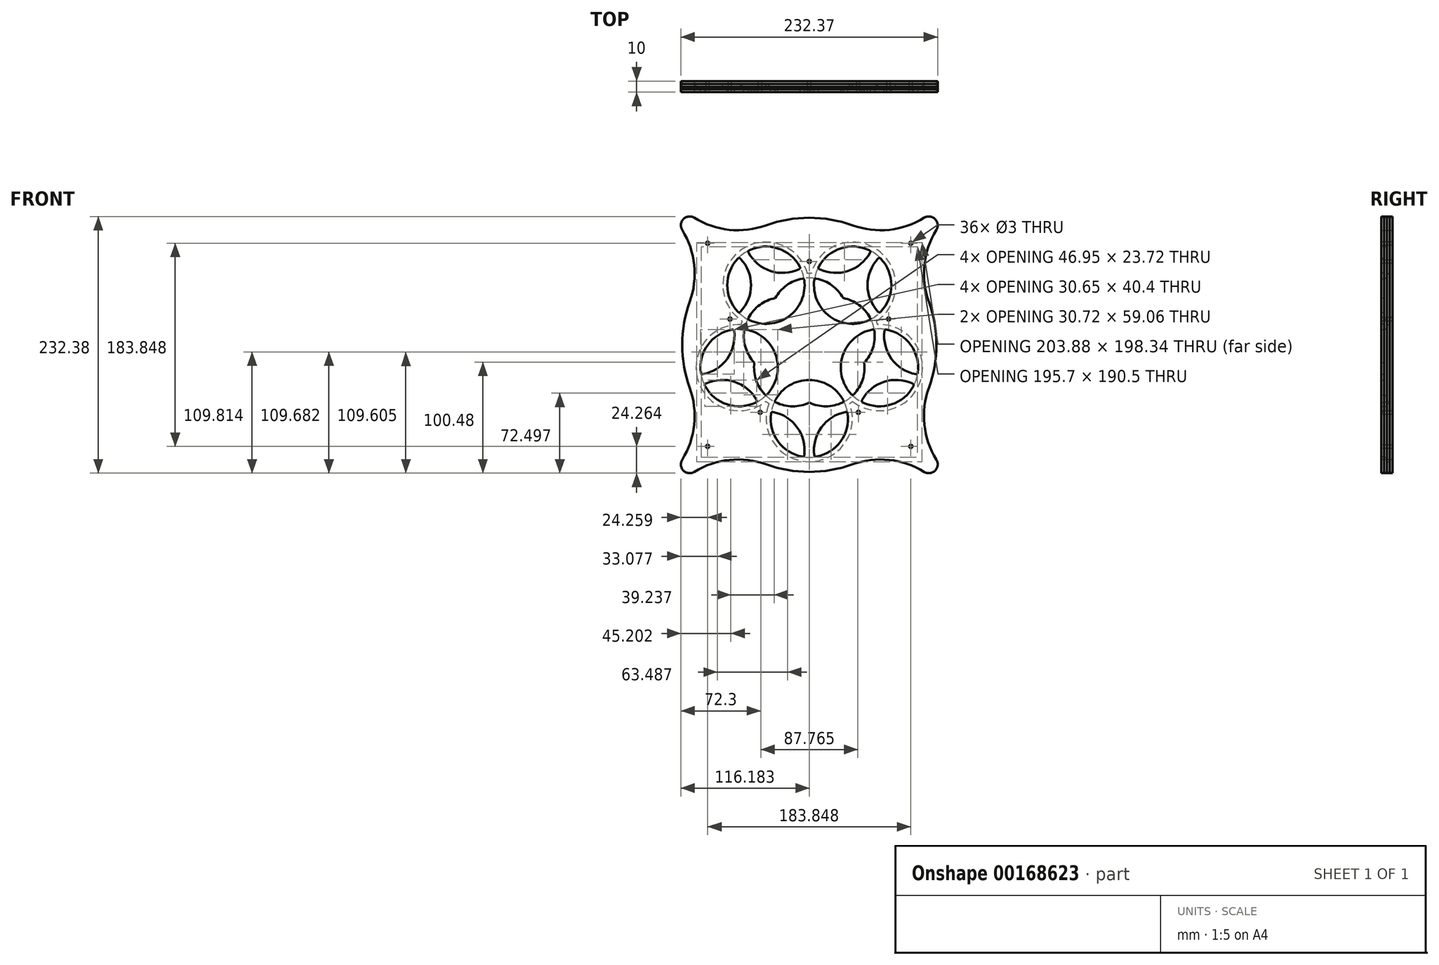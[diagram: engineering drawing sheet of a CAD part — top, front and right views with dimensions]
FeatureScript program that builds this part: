
annotation { "Feature Type Name" : "Feature", "Feature Type Description" : "" }
export const myFeature = defineFeature(function(context is Context, id is Id, definition is map)
    precondition{}
    {
        {
            var Q0;
            Q0=qCreatedBy(makeId("Front.planeOp"),FACE);
            var sketch = newSketch(context, id + "F0", { "sketchPlane" : qUnion([Q0])});
            skCircle(sketch, "E0", {"center": v(0, 0) * mm, "radius": 35 * mm});
            skLineSegment(sketch, "E1", {"start": v(0, 0) * mm, "end": v(48.5, 0) * mm});
            skCircle(sketch, "E2", {"center": v(48.5, 0) * mm, "radius": 35 * mm});
            skCircle(sketch, "E3.3.0", {"center": v(-14.99, 46.13) * mm, "radius": 35 * mm});
            skCircle(sketch, "E3.4.0", {"center": v(-39.24, 28.5) * mm, "radius": 35 * mm});
            skCircle(sketch, "E3.7.0", {"center": v(-14.99, -46.13) * mm, "radius": 35 * mm});
            skLineSegment(sketch, "E4", {"start": v(-34.45, -6.16) * mm, "end": v(-4.78, 34.67) * mm, "construction": true});
            skCircle(sketch, "E5.MirrorC", {"center": v(9.26, 28.5) * mm, "radius": 35 * mm});
            skLineSegment(sketch, "E6", {"start": v(0, 0) * mm, "end": v(9.26, 28.5) * mm});
            skLineSegment(sketch, "E7", {"start": v(0, 0) * mm, "end": v(-19.62, 14.25) * mm, "construction": true});
            skLineSegment(sketch, "E8", {"start": v(0, 0) * mm, "end": v(-29.97, 0) * mm, "construction": true});
            skCircle(sketch, "E9", {"center": v(-29.97, 0) * mm, "radius": 35 * mm});
            skLineSegment(sketch, "E10", {"start": v(24.25, 25.24) * mm, "end": v(24.25, -25.24) * mm, "construction": true});
            skCircle(sketch, "E11.MirrorC", {"center": v(63.49, -46.13) * mm, "radius": 35 * mm});
            skCircle(sketch, "E12.MirrorC", {"center": v(87.74, 28.5) * mm, "radius": 35 * mm});
            skLineSegment(sketch, "E13", {"start": v(-14.99, 31.63) * mm, "end": v(-14.99, -31.63) * mm, "construction": true});
            skCircle(sketch, "E14.MirrorC", {"center": v(-78.47, 0) * mm, "radius": 35 * mm});
            skSolve(sketch);
        }
        {
            var Q0;
            Q0=qCreatedBy(makeId("Front.planeOp"),FACE);
            var sketch = newSketch(context, id + "F1", { "sketchPlane" : qUnion([Q0])});
            skArc(sketch, "E15.0", {"start": v(-10.2, 80.8) * mm, "mid": v(-14.99, 81.13) * mm, "end": v(-19.77, 80.8) * mm});
            skArc(sketch, "E15.1", {"start": v(40.76, 43.77) * mm, "mid": v(42.55, 39.32) * mm, "end": v(43.72, 34.67) * mm});
            skArc(sketch, "E15.2", {"start": v(-70.73, 43.77) * mm, "mid": v(-72.52, 39.32) * mm, "end": v(-73.7, 34.67) * mm});
            skArc(sketch, "E15.3", {"start": v(-54.22, -25.24) * mm, "mid": v(-50.55, -28.32) * mm, "end": v(-46.48, -30.86) * mm});
            skArc(sketch, "E15.4", {"start": v(16.5, -30.86) * mm, "mid": v(20.57, -28.32) * mm, "end": v(24.25, -25.24) * mm});
            skArc(sketch, "E15.5", {"start": v(-46.48, -30.86) * mm, "mid": v(-14.99, -81.13) * mm, "end": v(16.5, -30.86) * mm});
            skLineSegment(sketch, "E16", {"start": v(-64.69, 4.48) * mm, "end": v(42.55, 39.32) * mm, "construction": true});
            skLineSegment(sketch, "E17", {"start": v(34.71, 4.48) * mm, "end": v(-72.52, 39.32) * mm, "construction": true});
            skPoint(sketch, "E18", {"position": v(-14.99, 20.63) * mm});
            skArc(sketch, "E19.1.0", {"start": v(24.25, -25.24) * mm, "mid": v(81.79, -10.82) * mm, "end": v(43.72, 34.67) * mm});
            skArc(sketch, "E19.2.0", {"start": v(40.76, 43.77) * mm, "mid": v(44.82, 102.95) * mm, "end": v(-10.2, 80.8) * mm});
            skArc(sketch, "E19.3.0", {"start": v(-19.77, 80.8) * mm, "mid": v(-74.8, 102.95) * mm, "end": v(-70.73, 43.77) * mm});
            skArc(sketch, "E19.4.0", {"start": v(-73.7, 34.67) * mm, "mid": v(-111.76, -10.82) * mm, "end": v(-54.22, -25.24) * mm});
            skLineSegment(sketch, "E20", {"start": v(-14.99, 20.63) * mm, "end": v(-14.99, -81.13) * mm, "construction": true});
            skLineSegment(sketch, "E21", {"start": v(-14.99, 20.63) * mm, "end": v(93.2, -87.56) * mm, "construction": true});
            skArc(sketch, "E22", {"start": v(88.99, -94.36) * mm, "mid": v(98.86, -93.22) * mm, "end": v(100, -83.34) * mm});
            skArc(sketch, "E23", {"start": v(93.2, -18.38) * mm, "mid": v(100.01, 20.63) * mm, "end": v(93.2, 59.64) * mm});
            skArc(sketch, "E24", {"start": v(93.2, -18.38) * mm, "mid": v(89.15, -51.64) * mm, "end": v(100, -83.34) * mm});
            skArc(sketch, "E25.MirrorCS", {"start": v(24.03, -87.55) * mm, "mid": v(57.29, -83.51) * mm, "end": v(88.99, -94.36) * mm});
            skArc(sketch, "E26.1.0", {"start": v(93.2, 59.64) * mm, "mid": v(89.15, 92.9) * mm, "end": v(100, 124.6) * mm});
            skArc(sketch, "E26.1.1", {"start": v(100, 124.6) * mm, "mid": v(98.86, 134.47) * mm, "end": v(88.99, 135.62) * mm});
            skArc(sketch, "E26.1.2", {"start": v(24.03, 128.8) * mm, "mid": v(57.29, 124.77) * mm, "end": v(88.99, 135.62) * mm});
            skArc(sketch, "E26.2.0", {"start": v(-54, 128.8) * mm, "mid": v(-87.26, 124.77) * mm, "end": v(-118.96, 135.62) * mm});
            skArc(sketch, "E26.2.1", {"start": v(-118.96, 135.62) * mm, "mid": v(-128.83, 134.47) * mm, "end": v(-129.97, 124.6) * mm});
            skArc(sketch, "E26.2.2", {"start": v(-123.17, 59.64) * mm, "mid": v(-119.13, 92.9) * mm, "end": v(-129.97, 124.6) * mm});
            skArc(sketch, "E26.3.0", {"start": v(-123.17, -18.38) * mm, "mid": v(-119.13, -51.64) * mm, "end": v(-129.97, -83.34) * mm});
            skArc(sketch, "E26.3.1", {"start": v(-129.97, -83.34) * mm, "mid": v(-128.83, -93.22) * mm, "end": v(-118.96, -94.36) * mm});
            skArc(sketch, "E26.3.2", {"start": v(-54, -87.55) * mm, "mid": v(-87.26, -83.51) * mm, "end": v(-118.96, -94.36) * mm});
            skArc(sketch, "E27.trimOffspring", {"start": v(-54, -87.55) * mm, "mid": v(-14.99, -94.37) * mm, "end": v(24.03, -87.55) * mm});
            skArc(sketch, "E28.trimOffspring", {"start": v(-123.17, 59.64) * mm, "mid": v(-129.99, 20.63) * mm, "end": v(-123.17, -18.38) * mm});
            skArc(sketch, "E29.trimOffspring", {"start": v(24.03, 128.8) * mm, "mid": v(-14.99, 135.63) * mm, "end": v(-54, 128.8) * mm});
            skSolve(sketch);
        }
        {
            var Q0;
            Q0=makeQuery(id+"F1.imprint","IMPRINT",FACE,{"disambiguationData":[TD([[makeQuery(id+"F1.imprint","IMPRINT",EDGE,{"derivedFrom":sQuery(id+"F1.wireOp",EDGE,"E15.0")}),-1.0]])]});
            var Q1;
            Q1=makeQuery(id+"F1.imprint","IMPRINT",FACE,{"disambiguationData":[TD([[makeQuery(id+"F1.imprint","IMPRINT",EDGE,{"derivedFrom":sQuery(id+"F1.wireOp",EDGE,"E15.0")}),1.0]])]});
            extrude(context, id + "F2", {"entities" : qUnion([Q0, Q1]), "depth" : 2.5 * mm});
        }
        {
            var Q0;
            Q0=makeQuery(id+"F2.opExtrude","CAP_FACE",FACE,{"disambiguationData":[OSD([sQuery(id+"F1.wireOp",EDGE,"E22"),sQuery(id+"F1.wireOp",EDGE,"E23"),sQuery(id+"F1.wireOp",EDGE,"E24"),sQuery(id+"F1.wireOp",EDGE,"E25.MirrorCS"),sQuery(id+"F1.wireOp",EDGE,"E26.1.0"),sQuery(id+"F1.wireOp",EDGE,"E26.1.1"),sQuery(id+"F1.wireOp",EDGE,"E26.1.2"),sQuery(id+"F1.wireOp",EDGE,"E26.2.0"),sQuery(id+"F1.wireOp",EDGE,"E26.2.1"),sQuery(id+"F1.wireOp",EDGE,"E26.2.2"),sQuery(id+"F1.wireOp",EDGE,"E26.3.0"),sQuery(id+"F1.wireOp",EDGE,"E26.3.1"),sQuery(id+"F1.wireOp",EDGE,"E26.3.2"),sQuery(id+"F1.wireOp",EDGE,"E27.trimOffspring"),sQuery(id+"F1.wireOp",EDGE,"E28.trimOffspring"),sQuery(id+"F1.wireOp",EDGE,"E29.trimOffspring")])],"isStart":false});
            var sketch = newSketch(context, id + "F3", { "sketchPlane" : qUnion([Q0])});
            skArc(sketch, "E30.0", {"start": v(-46.48, -30.86) * mm, "mid": v(-14.99, -81.13) * mm, "end": v(16.5, -30.86) * mm, "construction": true});
            skArc(sketch, "E31.0", {"start": v(24.25, -25.24) * mm, "mid": v(81.79, -10.82) * mm, "end": v(43.72, 34.67) * mm, "construction": true});
            skArc(sketch, "E32.0", {"start": v(40.76, 43.77) * mm, "mid": v(44.82, 102.95) * mm, "end": v(-10.2, 80.8) * mm, "construction": true});
            skArc(sketch, "E33.0", {"start": v(-19.77, 80.8) * mm, "mid": v(-74.8, 102.95) * mm, "end": v(-70.73, 43.77) * mm, "construction": true});
            skArc(sketch, "E34.0", {"start": v(-73.7, 34.67) * mm, "mid": v(-111.76, -10.82) * mm, "end": v(-54.22, -25.24) * mm, "construction": true});
            skArc(sketch, "E35.0", {"start": v(-70.73, 43.77) * mm, "mid": v(-72.52, 39.32) * mm, "end": v(-73.7, 34.67) * mm, "construction": true});
            skArc(sketch, "E36.0", {"start": v(-10.2, 80.8) * mm, "mid": v(-14.99, 81.13) * mm, "end": v(-19.77, 80.8) * mm, "construction": true});
            skArc(sketch, "E37.0", {"start": v(40.76, 43.77) * mm, "mid": v(42.55, 39.32) * mm, "end": v(43.72, 34.67) * mm, "construction": true});
            skArc(sketch, "E38.0", {"start": v(16.5, -30.86) * mm, "mid": v(20.57, -28.32) * mm, "end": v(24.25, -25.24) * mm, "construction": true});
            skArc(sketch, "E39.0", {"start": v(-54.22, -25.24) * mm, "mid": v(-50.55, -28.32) * mm, "end": v(-46.48, -30.86) * mm, "construction": true});
            skArc(sketch, "E40.0", {"start": v(-54.22, -30.54) * mm, "mid": v(-52.9, -31.55) * mm, "end": v(-51.53, -32.5) * mm});
            skArc(sketch, "E40.1", {"start": v(-76.8, 38.96) * mm, "mid": v(-115.57, -12.05) * mm, "end": v(-54.22, -30.54) * mm});
            skArc(sketch, "E40.2", {"start": v(-51.53, -32.5) * mm, "mid": v(-14.99, -85.13) * mm, "end": v(21.56, -32.5) * mm});
            skArc(sketch, "E40.3", {"start": v(-75.78, 42.13) * mm, "mid": v(-76.33, 40.56) * mm, "end": v(-76.8, 38.96) * mm});
            skArc(sketch, "E40.4", {"start": v(-16.65, 85.1) * mm, "mid": v(-77.15, 106.19) * mm, "end": v(-75.78, 42.13) * mm});
            skArc(sketch, "E40.5", {"start": v(-13.32, 85.1) * mm, "mid": v(-14.99, 85.13) * mm, "end": v(-16.65, 85.1) * mm});
            skArc(sketch, "E40.6", {"start": v(21.56, -32.5) * mm, "mid": v(22.92, -31.55) * mm, "end": v(24.25, -30.54) * mm});
            skArc(sketch, "E40.7", {"start": v(24.25, -30.54) * mm, "mid": v(85.6, -12.05) * mm, "end": v(46.83, 38.96) * mm});
            skArc(sketch, "E40.8", {"start": v(45.8, 42.13) * mm, "mid": v(46.35, 40.56) * mm, "end": v(46.83, 38.96) * mm});
            skArc(sketch, "E40.9", {"start": v(45.8, 42.13) * mm, "mid": v(47.17, 106.19) * mm, "end": v(-13.32, 85.1) * mm});
            skSolve(sketch);
        }
        {
            var Q0;
            Q0=makeQuery(id+"F3.imprint","IMPRINT",FACE,{"disambiguationData":[TD([[makeQuery(id+"F3.imprint","IMPRINT",EDGE,{"derivedFrom":sQuery(id+"F3.wireOp",EDGE,"E40.0")}),-1.0]])]});
            extrude(context, id + "F4", {"entities" : qUnion([Q0]), "depth" : 2.5 * mm});
        }
        {
            var Q0;
            Q0=makeQuery(id+"F4.opExtrude","CAP_FACE",FACE,{"disambiguationData":[OSD([sQuery(id+"F1.wireOp",EDGE,"E22"),sQuery(id+"F1.wireOp",EDGE,"E23"),sQuery(id+"F1.wireOp",EDGE,"E24"),sQuery(id+"F1.wireOp",EDGE,"E25.MirrorCS"),sQuery(id+"F1.wireOp",EDGE,"E26.1.0"),sQuery(id+"F1.wireOp",EDGE,"E26.1.1"),sQuery(id+"F1.wireOp",EDGE,"E26.1.2"),sQuery(id+"F1.wireOp",EDGE,"E26.2.0"),sQuery(id+"F1.wireOp",EDGE,"E26.2.1"),sQuery(id+"F1.wireOp",EDGE,"E26.2.2"),sQuery(id+"F1.wireOp",EDGE,"E26.3.0"),sQuery(id+"F1.wireOp",EDGE,"E26.3.1"),sQuery(id+"F1.wireOp",EDGE,"E26.3.2"),sQuery(id+"F1.wireOp",EDGE,"E27.trimOffspring"),sQuery(id+"F1.wireOp",EDGE,"E28.trimOffspring"),sQuery(id+"F1.wireOp",EDGE,"E29.trimOffspring"),sQuery(id+"F3.wireOp",EDGE,"E40.0"),sQuery(id+"F3.wireOp",EDGE,"E40.1"),sQuery(id+"F3.wireOp",EDGE,"E40.2"),sQuery(id+"F3.wireOp",EDGE,"E40.3"),sQuery(id+"F3.wireOp",EDGE,"E40.4"),sQuery(id+"F3.wireOp",EDGE,"E40.5"),sQuery(id+"F3.wireOp",EDGE,"E40.6"),sQuery(id+"F3.wireOp",EDGE,"E40.7"),sQuery(id+"F3.wireOp",EDGE,"E40.8"),sQuery(id+"F3.wireOp",EDGE,"E40.9")])],"isStart":false});
            var sketch = newSketch(context, id + "F5", { "sketchPlane" : qUnion([Q0])});
            skArc(sketch, "E41.0", {"start": v(-123.17, 59.64) * mm, "mid": v(-129.99, 20.63) * mm, "end": v(-123.17, -18.38) * mm});
            skArc(sketch, "E41.1", {"start": v(-123.17, 59.64) * mm, "mid": v(-119.13, 92.9) * mm, "end": v(-129.97, 124.6) * mm});
            skArc(sketch, "E41.2", {"start": v(-118.96, 135.62) * mm, "mid": v(-128.83, 134.47) * mm, "end": v(-129.97, 124.6) * mm});
            skArc(sketch, "E41.3", {"start": v(-54, 128.8) * mm, "mid": v(-87.26, 124.77) * mm, "end": v(-118.96, 135.62) * mm});
            skArc(sketch, "E41.4", {"start": v(24.03, 128.8) * mm, "mid": v(-14.99, 135.63) * mm, "end": v(-54, 128.8) * mm});
            skArc(sketch, "E41.5", {"start": v(24.03, 128.8) * mm, "mid": v(57.29, 124.77) * mm, "end": v(88.99, 135.62) * mm});
            skArc(sketch, "E41.6", {"start": v(100, 124.6) * mm, "mid": v(98.86, 134.47) * mm, "end": v(88.99, 135.62) * mm});
            skArc(sketch, "E41.7", {"start": v(93.2, 59.64) * mm, "mid": v(89.15, 92.9) * mm, "end": v(100, 124.6) * mm});
            skArc(sketch, "E41.8", {"start": v(93.2, -18.38) * mm, "mid": v(100.01, 20.63) * mm, "end": v(93.2, 59.64) * mm});
            skArc(sketch, "E41.9", {"start": v(93.2, -18.38) * mm, "mid": v(89.15, -51.64) * mm, "end": v(100, -83.34) * mm});
            skArc(sketch, "E41.10", {"start": v(88.99, -94.36) * mm, "mid": v(98.86, -93.22) * mm, "end": v(100, -83.34) * mm});
            skArc(sketch, "E41.11", {"start": v(24.03, -87.55) * mm, "mid": v(57.29, -83.51) * mm, "end": v(88.99, -94.36) * mm});
            skArc(sketch, "E41.12", {"start": v(-54, -87.55) * mm, "mid": v(-14.99, -94.37) * mm, "end": v(24.03, -87.55) * mm});
            skArc(sketch, "E41.13", {"start": v(-54, -87.55) * mm, "mid": v(-87.26, -83.51) * mm, "end": v(-118.96, -94.36) * mm});
            skArc(sketch, "E41.14", {"start": v(-129.97, -83.34) * mm, "mid": v(-128.83, -93.22) * mm, "end": v(-118.96, -94.36) * mm});
            skArc(sketch, "E41.15", {"start": v(-123.17, -18.38) * mm, "mid": v(-119.13, -51.64) * mm, "end": v(-129.97, -83.34) * mm});
            skArc(sketch, "E42.0", {"start": v(-70.73, 43.77) * mm, "mid": v(-72.52, 39.32) * mm, "end": v(-73.7, 34.67) * mm});
            skArc(sketch, "E42.1", {"start": v(-19.77, 80.8) * mm, "mid": v(-74.8, 102.95) * mm, "end": v(-70.73, 43.77) * mm});
            skArc(sketch, "E42.2", {"start": v(-10.2, 80.8) * mm, "mid": v(-14.99, 81.13) * mm, "end": v(-19.77, 80.8) * mm});
            skArc(sketch, "E42.3", {"start": v(40.76, 43.77) * mm, "mid": v(44.82, 102.95) * mm, "end": v(-10.2, 80.8) * mm});
            skArc(sketch, "E42.4", {"start": v(40.76, 43.77) * mm, "mid": v(42.55, 39.32) * mm, "end": v(43.72, 34.67) * mm});
            skArc(sketch, "E42.5", {"start": v(24.25, -25.24) * mm, "mid": v(81.79, -10.82) * mm, "end": v(43.72, 34.67) * mm});
            skArc(sketch, "E42.6", {"start": v(16.5, -30.86) * mm, "mid": v(20.57, -28.32) * mm, "end": v(24.25, -25.24) * mm});
            skArc(sketch, "E42.7", {"start": v(-46.48, -30.86) * mm, "mid": v(-14.99, -81.13) * mm, "end": v(16.5, -30.86) * mm});
            skArc(sketch, "E42.8", {"start": v(-54.22, -25.24) * mm, "mid": v(-50.55, -28.32) * mm, "end": v(-46.48, -30.86) * mm});
            skArc(sketch, "E42.9", {"start": v(-73.7, 34.67) * mm, "mid": v(-111.76, -10.82) * mm, "end": v(-54.22, -25.24) * mm});
            skSolve(sketch);
        }
        {
            var Q0;
            Q0 = qSketchRegion(id + "F5", true);
            extrude(context, id + "F6", {"entities" : qUnion([Q0]), "depth" : 2.5 * mm});
        }
        {
            var Q0;
            Q0=makeQuery(id+"F6.opExtrude","CAP_FACE",FACE,{"disambiguationData":[OSD([sQuery(id+"F5.wireOp",EDGE,"E41.0"),sQuery(id+"F5.wireOp",EDGE,"E41.1"),sQuery(id+"F5.wireOp",EDGE,"E41.2"),sQuery(id+"F5.wireOp",EDGE,"E41.3"),sQuery(id+"F5.wireOp",EDGE,"E41.4"),sQuery(id+"F5.wireOp",EDGE,"E41.5"),sQuery(id+"F5.wireOp",EDGE,"E41.6"),sQuery(id+"F5.wireOp",EDGE,"E41.7"),sQuery(id+"F5.wireOp",EDGE,"E41.8"),sQuery(id+"F5.wireOp",EDGE,"E41.9"),sQuery(id+"F5.wireOp",EDGE,"E41.10"),sQuery(id+"F5.wireOp",EDGE,"E41.11"),sQuery(id+"F5.wireOp",EDGE,"E41.12"),sQuery(id+"F5.wireOp",EDGE,"E41.13"),sQuery(id+"F5.wireOp",EDGE,"E41.14"),sQuery(id+"F5.wireOp",EDGE,"E41.15"),sQuery(id+"F5.wireOp",EDGE,"E42.0"),sQuery(id+"F5.wireOp",EDGE,"E42.1"),sQuery(id+"F5.wireOp",EDGE,"E42.2"),sQuery(id+"F5.wireOp",EDGE,"E42.3"),sQuery(id+"F5.wireOp",EDGE,"E42.4"),sQuery(id+"F5.wireOp",EDGE,"E42.5"),sQuery(id+"F5.wireOp",EDGE,"E42.6"),sQuery(id+"F5.wireOp",EDGE,"E42.7"),sQuery(id+"F5.wireOp",EDGE,"E42.8"),sQuery(id+"F5.wireOp",EDGE,"E42.9")])],"isStart":false});
            var sketch = newSketch(context, id + "F7", { "sketchPlane" : qUnion([Q0])});
            skArc(sketch, "E43.0", {"start": v(-123.17, 59.64) * mm, "mid": v(-129.99, 20.63) * mm, "end": v(-123.17, -18.38) * mm});
            skArc(sketch, "E43.1", {"start": v(-123.17, 59.64) * mm, "mid": v(-119.13, 92.9) * mm, "end": v(-129.97, 124.6) * mm});
            skArc(sketch, "E43.2", {"start": v(-118.96, 135.62) * mm, "mid": v(-128.83, 134.47) * mm, "end": v(-129.97, 124.6) * mm});
            skArc(sketch, "E43.3", {"start": v(-54, 128.8) * mm, "mid": v(-87.26, 124.77) * mm, "end": v(-118.96, 135.62) * mm});
            skArc(sketch, "E43.4", {"start": v(24.03, 128.8) * mm, "mid": v(-14.99, 135.63) * mm, "end": v(-54, 128.8) * mm});
            skArc(sketch, "E43.5", {"start": v(24.03, 128.8) * mm, "mid": v(57.29, 124.77) * mm, "end": v(88.99, 135.62) * mm});
            skArc(sketch, "E43.6", {"start": v(100, 124.6) * mm, "mid": v(98.86, 134.47) * mm, "end": v(88.99, 135.62) * mm});
            skArc(sketch, "E43.7", {"start": v(93.2, 59.64) * mm, "mid": v(89.15, 92.9) * mm, "end": v(100, 124.6) * mm});
            skArc(sketch, "E43.8", {"start": v(93.2, -18.38) * mm, "mid": v(100.01, 20.63) * mm, "end": v(93.2, 59.64) * mm});
            skArc(sketch, "E43.9", {"start": v(93.2, -18.38) * mm, "mid": v(89.15, -51.64) * mm, "end": v(100, -83.34) * mm});
            skArc(sketch, "E43.10", {"start": v(88.99, -94.36) * mm, "mid": v(98.86, -93.22) * mm, "end": v(100, -83.34) * mm});
            skArc(sketch, "E43.11", {"start": v(24.03, -87.55) * mm, "mid": v(57.29, -83.51) * mm, "end": v(88.99, -94.36) * mm});
            skArc(sketch, "E43.12", {"start": v(-54, -87.55) * mm, "mid": v(-14.99, -94.37) * mm, "end": v(24.03, -87.55) * mm});
            skArc(sketch, "E43.13", {"start": v(-54, -87.55) * mm, "mid": v(-87.26, -83.51) * mm, "end": v(-118.96, -94.36) * mm});
            skArc(sketch, "E43.14", {"start": v(-129.97, -83.34) * mm, "mid": v(-128.83, -93.22) * mm, "end": v(-118.96, -94.36) * mm});
            skArc(sketch, "E43.15", {"start": v(-123.17, -18.38) * mm, "mid": v(-119.13, -51.64) * mm, "end": v(-129.97, -83.34) * mm});
            skArc(sketch, "E43.21", {"start": v(33.36, -31.56) * mm, "mid": v(59.32, -33.29) * mm, "end": v(79.3, -16.63) * mm});
            skArc(sketch, "E44.0", {"start": v(25.34, -24.15) * mm, "mid": v(33.26, -10.9) * mm, "end": v(34.71, 4.48) * mm});
            skArc(sketch, "E45.0", {"start": v(43.95, 33.15) * mm, "mid": v(42.58, 17.77) * mm, "end": v(34.71, 4.48) * mm});
            skArc(sketch, "E46.0", {"start": v(81.43, -5.92) * mm, "mid": v(59.42, 7.94) * mm, "end": v(53.05, 33.15) * mm});
            skArc(sketch, "E47.0", {"start": v(32.7, -29.5) * mm, "mid": v(52.67, -12.84) * mm, "end": v(78.62, -14.57) * mm});
            skArc(sketch, "E48.trimOffspring", {"start": v(83.2, -4.64) * mm, "mid": v(76.82, 20.57) * mm, "end": v(54.8, 34.43) * mm});
            skPoint(sketch, "E43.19.end.orphan", {"position": v(-10.2, 80.8) * mm});
            skPoint(sketch, "E43.19.start.orphan", {"position": v(40.76, 43.77) * mm});
            skPoint(sketch, "E43.18.end.orphan", {"position": v(-19.77, 80.8) * mm});
            skPoint(sketch, "E43.18.start.orphan", {"position": v(-10.2, 80.8) * mm});
            skPoint(sketch, "E43.17.end.orphan", {"position": v(-70.73, 43.77) * mm});
            skPoint(sketch, "E43.17.start.orphan", {"position": v(-19.77, 80.8) * mm});
            skPoint(sketch, "E43.16.end.orphan", {"position": v(-73.7, 34.67) * mm});
            skPoint(sketch, "E43.16.start.orphan", {"position": v(-70.73, 43.77) * mm});
            skPoint(sketch, "E43.25.end.orphan", {"position": v(-54.22, -25.24) * mm});
            skPoint(sketch, "E43.25.start.orphan", {"position": v(-73.7, 34.67) * mm});
            skPoint(sketch, "E43.24.end.orphan", {"position": v(-46.48, -30.86) * mm});
            skPoint(sketch, "E43.24.start.orphan", {"position": v(-54.22, -25.24) * mm});
            skPoint(sketch, "E43.23.end.orphan", {"position": v(16.5, -30.86) * mm});
            skPoint(sketch, "E43.23.start.orphan", {"position": v(-46.48, -30.86) * mm});
            skPoint(sketch, "E43.22.start.orphan", {"position": v(16.5, -30.86) * mm});
            skPoint(sketch, "E43.20.end.orphan", {"position": v(43.72, 34.67) * mm});
            skPoint(sketch, "E43.20.start.orphan", {"position": v(40.76, 43.77) * mm});
            skArc(sketch, "E49.trimOffspring", {"start": v(42.2, 34.43) * mm, "mid": v(15.21, 10.82) * mm, "end": v(23.16, -24.15) * mm});
            skPoint(sketch, "E50.visualSharp", {"position": v(24.25, -25.24) * mm});
            skArc(sketch, "E50.filletArc", {"start": v(23.16, -24.15) * mm, "mid": v(24.25, -24.61) * mm, "end": v(25.34, -24.15) * mm});
            skArc(sketch, "E51.filletArc", {"start": v(43.95, 33.15) * mm, "mid": v(43.35, 34.17) * mm, "end": v(42.2, 34.43) * mm});
            skPoint(sketch, "E52.visualSharp", {"position": v(53.28, 34.67) * mm});
            skArc(sketch, "E52.filletArc", {"start": v(54.8, 34.43) * mm, "mid": v(53.65, 34.17) * mm, "end": v(53.05, 33.15) * mm});
            skPoint(sketch, "E53.visualSharp", {"position": v(82.95, -6.16) * mm});
            skArc(sketch, "E53.filletArc", {"start": v(81.43, -5.92) * mm, "mid": v(82.59, -5.66) * mm, "end": v(83.2, -4.64) * mm});
            skPoint(sketch, "E54.visualSharp", {"position": v(80, -15.26) * mm});
            skArc(sketch, "E54.filletArc", {"start": v(79.3, -16.63) * mm, "mid": v(79.4, -15.46) * mm, "end": v(78.62, -14.57) * mm});
            skPoint(sketch, "E55.visualSharp", {"position": v(32, -30.86) * mm});
            skArc(sketch, "E55.filletArc", {"start": v(32.7, -29.5) * mm, "mid": v(32.59, -30.67) * mm, "end": v(33.36, -31.56) * mm});
            skPoint(sketch, "E56.1.0", {"position": v(48.5, 99.87) * mm});
            skArc(sketch, "E56.1.1", {"start": v(40.06, 104.13) * mm, "mid": v(20.08, 87.47) * mm, "end": v(-5.87, 89.2) * mm});
            skArc(sketch, "E56.1.2", {"start": v(47.41, 50.49) * mm, "mid": v(37.75, 74.63) * mm, "end": v(47.41, 98.78) * mm});
            skArc(sketch, "E56.1.3", {"start": v(-8.68, 80.55) * mm, "mid": v(5.52, 74.5) * mm, "end": v(15.73, 62.9) * mm});
            skArc(sketch, "E56.1.4", {"start": v(-10.44, 79.28) * mm, "mid": v(3.68, 46.32) * mm, "end": v(39.39, 43.08) * mm});
            skPoint(sketch, "E56.1.6", {"position": v(-7.25, 89.9) * mm});
            skPoint(sketch, "E56.1.7", {"position": v(48.5, 49.4) * mm});
            skArc(sketch, "E56.1.9", {"start": v(39.39, 106.2) * mm, "mid": v(13.43, 107.92) * mm, "end": v(-6.54, 91.27) * mm});
            skArc(sketch, "E56.1.10", {"start": v(40.06, 45.14) * mm, "mid": v(29.9, 56.77) * mm, "end": v(15.73, 62.9) * mm});
            skArc(sketch, "E56.1.11", {"start": v(49.59, 50.49) * mm, "mid": v(59.25, 74.63) * mm, "end": v(49.59, 98.78) * mm});
            skPoint(sketch, "E56.1.14", {"position": v(40.76, 105.5) * mm});
            skArc(sketch, "E56.1.16", {"start": v(49.59, 98.78) * mm, "mid": v(48.5, 99.25) * mm, "end": v(47.41, 98.78) * mm});
            skArc(sketch, "E56.1.17", {"start": v(-8.68, 80.55) * mm, "mid": v(-9.84, 80.3) * mm, "end": v(-10.44, 79.28) * mm});
            skArc(sketch, "E56.1.18", {"start": v(47.41, 50.49) * mm, "mid": v(48.5, 50.02) * mm, "end": v(49.59, 50.49) * mm});
            skArc(sketch, "E56.1.19", {"start": v(-6.54, 91.27) * mm, "mid": v(-6.65, 90.1) * mm, "end": v(-5.87, 89.2) * mm});
            skArc(sketch, "E56.1.20", {"start": v(39.39, 43.08) * mm, "mid": v(40.16, 43.97) * mm, "end": v(40.06, 45.14) * mm});
            skPoint(sketch, "E56.2.0", {"position": v(-70.73, 105.5) * mm});
            skArc(sketch, "E56.2.1", {"start": v(-77.39, 98.78) * mm, "mid": v(-67.72, 74.63) * mm, "end": v(-77.39, 50.49) * mm});
            skArc(sketch, "E56.2.2", {"start": v(-24.1, 89.2) * mm, "mid": v(-50.05, 87.47) * mm, "end": v(-70.03, 104.13) * mm});
            skArc(sketch, "E56.2.3", {"start": v(-70.03, 45.14) * mm, "mid": v(-59.88, 56.77) * mm, "end": v(-45.7, 62.9) * mm});
            skArc(sketch, "E56.2.4", {"start": v(-69.36, 43.08) * mm, "mid": v(-33.65, 46.32) * mm, "end": v(-19.53, 79.28) * mm});
            skPoint(sketch, "E56.2.6", {"position": v(-78.47, 49.4) * mm});
            skPoint(sketch, "E56.2.7", {"position": v(-22.73, 89.9) * mm});
            skArc(sketch, "E56.2.9", {"start": v(-79.56, 98.78) * mm, "mid": v(-89.22, 74.63) * mm, "end": v(-79.56, 50.49) * mm});
            skArc(sketch, "E56.2.10", {"start": v(-21.3, 80.55) * mm, "mid": v(-35.5, 74.5) * mm, "end": v(-45.7, 62.9) * mm});
            skArc(sketch, "E56.2.11", {"start": v(-23.43, 91.27) * mm, "mid": v(-43.4, 107.92) * mm, "end": v(-69.36, 106.2) * mm});
            skPoint(sketch, "E56.2.14", {"position": v(-78.47, 99.87) * mm});
            skArc(sketch, "E56.2.16", {"start": v(-69.36, 106.2) * mm, "mid": v(-70.14, 105.3) * mm, "end": v(-70.03, 104.13) * mm});
            skArc(sketch, "E56.2.17", {"start": v(-70.03, 45.14) * mm, "mid": v(-70.14, 43.97) * mm, "end": v(-69.36, 43.08) * mm});
            skArc(sketch, "E56.2.18", {"start": v(-24.1, 89.2) * mm, "mid": v(-23.32, 90.1) * mm, "end": v(-23.43, 91.27) * mm});
            skArc(sketch, "E56.2.19", {"start": v(-79.56, 50.49) * mm, "mid": v(-78.47, 50.02) * mm, "end": v(-77.39, 50.49) * mm});
            skArc(sketch, "E56.2.20", {"start": v(-19.53, 79.28) * mm, "mid": v(-20.14, 80.3) * mm, "end": v(-21.3, 80.55) * mm});
            skPoint(sketch, "E56.3.0", {"position": v(-112.93, -6.16) * mm});
            skArc(sketch, "E56.3.1", {"start": v(-108.6, -14.57) * mm, "mid": v(-82.65, -12.84) * mm, "end": v(-62.67, -29.5) * mm});
            skArc(sketch, "E56.3.2", {"start": v(-83.02, 33.15) * mm, "mid": v(-89.4, 7.94) * mm, "end": v(-111.4, -5.92) * mm});
            skArc(sketch, "E56.3.3", {"start": v(-55.31, -24.15) * mm, "mid": v(-63.24, -10.9) * mm, "end": v(-64.69, 4.48) * mm});
            skArc(sketch, "E56.3.4", {"start": v(-53.14, -24.15) * mm, "mid": v(-45.19, 10.82) * mm, "end": v(-72.17, 34.43) * mm});
            skPoint(sketch, "E56.3.6", {"position": v(-61.97, -30.86) * mm});
            skPoint(sketch, "E56.3.7", {"position": v(-83.26, 34.67) * mm});
            skArc(sketch, "E56.3.9", {"start": v(-109.27, -16.63) * mm, "mid": v(-89.3, -33.29) * mm, "end": v(-63.34, -31.56) * mm});
            skArc(sketch, "E56.3.10", {"start": v(-73.93, 33.15) * mm, "mid": v(-72.55, 17.77) * mm, "end": v(-64.69, 4.48) * mm});
            skArc(sketch, "E56.3.11", {"start": v(-84.78, 34.43) * mm, "mid": v(-106.8, 20.57) * mm, "end": v(-113.17, -4.64) * mm});
            skPoint(sketch, "E56.3.14", {"position": v(-109.97, -15.26) * mm});
            skArc(sketch, "E56.3.16", {"start": v(-113.17, -4.64) * mm, "mid": v(-112.56, -5.66) * mm, "end": v(-111.4, -5.92) * mm});
            skArc(sketch, "E56.3.17", {"start": v(-55.31, -24.15) * mm, "mid": v(-54.22, -24.61) * mm, "end": v(-53.14, -24.15) * mm});
            skArc(sketch, "E56.3.18", {"start": v(-83.02, 33.15) * mm, "mid": v(-83.63, 34.17) * mm, "end": v(-84.78, 34.43) * mm});
            skArc(sketch, "E56.3.19", {"start": v(-63.34, -31.56) * mm, "mid": v(-62.56, -30.67) * mm, "end": v(-62.67, -29.5) * mm});
            skArc(sketch, "E56.3.20", {"start": v(-72.17, 34.43) * mm, "mid": v(-73.32, 34.17) * mm, "end": v(-73.93, 33.15) * mm});
            skPoint(sketch, "E56.4.0", {"position": v(-19.77, -80.8) * mm});
            skArc(sketch, "E56.4.1", {"start": v(-10.44, -79.28) * mm, "mid": v(-4.07, -54.06) * mm, "end": v(17.95, -40.2) * mm});
            skArc(sketch, "E56.4.2", {"start": v(-47.92, -40.2) * mm, "mid": v(-25.9, -54.06) * mm, "end": v(-19.53, -79.28) * mm});
            skArc(sketch, "E56.4.3", {"start": v(15.14, -31.56) * mm, "mid": v(0.08, -35) * mm, "end": v(-14.99, -31.63) * mm});
            skArc(sketch, "E56.4.4", {"start": v(15.8, -29.5) * mm, "mid": v(-14.99, -11.13) * mm, "end": v(-45.78, -29.5) * mm});
            skPoint(sketch, "E56.4.6", {"position": v(19.47, -39.96) * mm});
            skPoint(sketch, "E56.4.7", {"position": v(-49.44, -39.96) * mm});
            skArc(sketch, "E56.4.9", {"start": v(-8.68, -80.55) * mm, "mid": v(13.33, -66.7) * mm, "end": v(19.7, -41.48) * mm});
            skArc(sketch, "E56.4.10", {"start": v(-45.11, -31.56) * mm, "mid": v(-30.06, -35) * mm, "end": v(-14.99, -31.63) * mm});
            skArc(sketch, "E56.4.11", {"start": v(-49.68, -41.48) * mm, "mid": v(-43.3, -66.7) * mm, "end": v(-21.3, -80.55) * mm});
            skPoint(sketch, "E56.4.14", {"position": v(-10.2, -80.8) * mm});
            skArc(sketch, "E56.4.16", {"start": v(-21.3, -80.55) * mm, "mid": v(-20.14, -80.3) * mm, "end": v(-19.53, -79.28) * mm});
            skArc(sketch, "E56.4.17", {"start": v(15.14, -31.56) * mm, "mid": v(15.91, -30.67) * mm, "end": v(15.8, -29.5) * mm});
            skArc(sketch, "E56.4.18", {"start": v(-47.92, -40.2) * mm, "mid": v(-49.07, -40.47) * mm, "end": v(-49.68, -41.48) * mm});
            skArc(sketch, "E56.4.19", {"start": v(19.7, -41.48) * mm, "mid": v(19.1, -40.47) * mm, "end": v(17.95, -40.2) * mm});
            skArc(sketch, "E56.4.20", {"start": v(-45.78, -29.5) * mm, "mid": v(-45.89, -30.67) * mm, "end": v(-45.11, -31.56) * mm});
            skArc(sketch, "E57.1.0", {"start": v(40.06, 104.13) * mm, "mid": v(40.16, 105.3) * mm, "end": v(39.39, 106.2) * mm});
            skArc(sketch, "E57.2.0", {"start": v(-77.39, 98.78) * mm, "mid": v(-78.47, 99.25) * mm, "end": v(-79.56, 98.78) * mm});
            skArc(sketch, "E57.3.0", {"start": v(-108.6, -14.57) * mm, "mid": v(-109.38, -15.46) * mm, "end": v(-109.27, -16.63) * mm});
            skArc(sketch, "E57.4.0", {"start": v(-10.44, -79.28) * mm, "mid": v(-9.84, -80.3) * mm, "end": v(-8.68, -80.55) * mm});
            skSolve(sketch);
        }
        {
            var Q0;
            Q0 = qSketchRegion(id + "F7", true);
            extrude(context, id + "F8", {"entities" : qUnion([Q0]), "depth" : 2.5 * mm});
        }
        {
            var Q0;
            Q0=qCreatedBy(makeId("Front.planeOp"),FACE);
            var sketch = newSketch(context, id + "F9", { "sketchPlane" : qUnion([Q0])});
            skLineSegment(sketch, "E58.0", {"start": v(-14.99, 20.63) * mm, "end": v(93.2, -87.56) * mm, "construction": true});
            skCircle(sketch, "E59", {"center": v(76.94, -71.3) * mm, "radius": 1.5 * mm});
            skCircle(sketch, "E60.1.0", {"center": v(76.94, 112.55) * mm, "radius": 1.5 * mm});
            skCircle(sketch, "E60.2.0", {"center": v(-106.91, 112.55) * mm, "radius": 1.5 * mm});
            skCircle(sketch, "E60.3.0", {"center": v(-106.91, -71.3) * mm, "radius": 1.5 * mm});
            skPoint(sketch, "E60.center", {"position": v(-14.99, 20.63) * mm});
            skLineSegment(sketch, "E61", {"start": v(-14.99, 20.63) * mm, "end": v(29.4, -40.45) * mm, "construction": true});
            skPoint(sketch, "E62", {"position": v(20.57, -28.32) * mm});
            skCircle(sketch, "E63", {"center": v(29.4, -40.45) * mm, "radius": 1.5 * mm});
            skCircle(sketch, "E64.1.0", {"center": v(56.82, 43.96) * mm, "radius": 1.5 * mm});
            skCircle(sketch, "E64.2.0", {"center": v(-14.99, 96.13) * mm, "radius": 1.5 * mm});
            skCircle(sketch, "E64.3.0", {"center": v(-86.8, 43.96) * mm, "radius": 1.5 * mm});
            skCircle(sketch, "E64.4.0", {"center": v(-59.37, -40.45) * mm, "radius": 1.5 * mm});
            skSolve(sketch);
        }
        {
            var Q0;
            Q0 = qSketchRegion(id + "F9", true);
            extrude(context, id + "F10", {"entities" : qUnion([Q0]), "operationType" : NewBodyOperationType.REMOVE, "depth" : 25 * mm});
        }
        {
            var Q0;
            Q0 = qSketchRegion(id + "F9", true);
            extrude(context, id + "F11", {"entities" : qUnion([Q0]), "operationType" : NewBodyOperationType.REMOVE, "endBound" : BoundingType.THROUGH_ALL, "oppositeDirection" : true, "depth" : 25 * mm});
        }
    });
